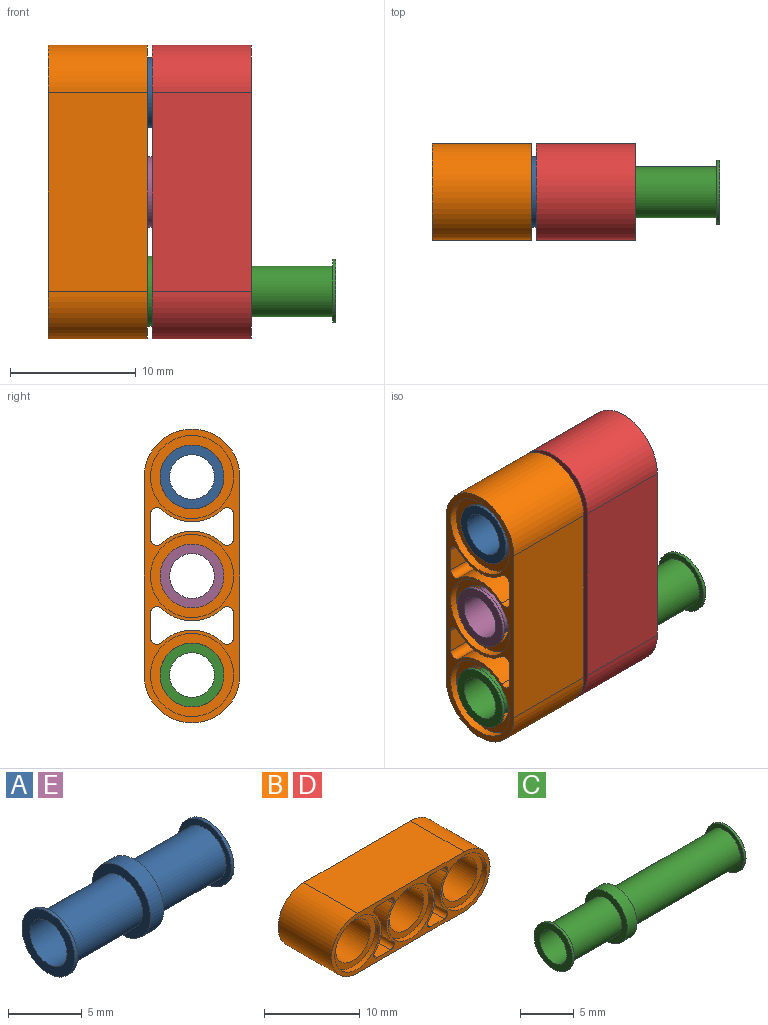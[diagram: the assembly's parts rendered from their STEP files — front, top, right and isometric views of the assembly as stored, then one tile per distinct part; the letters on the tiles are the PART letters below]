
ASSEMBLY  parts=5 mates=4
PART A: 12 faces, bbox 15.2x5.6x5.6 mm
  f0: cylinder r=2.54mm len=5.08mm, axis (-1,0,0), area 4.1mm2, adj f1,f11
  f1: plane 5.08x5.08mm, normal (1,0,0), area 7.3mm2, adj f0,f2
  f2: cylinder r=2.03mm len=6.73mm, axis (-1,0,0), area 85.9mm2, adj f1,f3
  f3: plane 5.59x5.59mm, normal (-1,0,0), area 11.6mm2, adj f2,f4
  f4: cylinder r=2.79mm len=5.59mm, axis (-1,0,0), area 22.3mm2, adj f3,f5
  f5: plane 5.59x5.59mm, normal (1,0,0), area 11.6mm2, adj f4,f6
  f6: cylinder r=2.03mm len=6.73mm, axis (-1,0,0), area 85.9mm2, adj f5,f7
  f7: plane 5.08x5.08mm, normal (-1,0,0), area 7.3mm2, adj f6,f8
  f8: cylinder r=2.54mm len=5.08mm, axis (-1,0,0), area 4.1mm2, adj f7,f9
  f9: plane 5.08x5.08mm, normal (1,0,0), area 10.3mm2, adj f8,f10
  f10: cylinder r=1.78mm len=15.24mm, axis (-1,0,0), area 170.3mm2, adj f9,f11
  f11: plane 5.08x5.08mm, normal (-1,0,0), area 10.3mm2, adj f0,f10
PART B: 37 faces, bbox 23.4x7.9x7.6 mm
  f0: cylinder r=2.54mm len=6.6mm, axis (0,-1,0), area 105.4mm2, adj f11,f32
  f1: plane 7.87x1.97mm, normal (0,0,1), area 15.5mm2, adj f2,f9,f24,f30
  f2: cylinder r=0.51mm len=7.87mm, axis (0,-1,0), area 9.3mm2, adj f1,f3,f9,f30
  f3: cylinder r=3.56mm len=7.87mm, axis (0,-1,0), area 42.5mm2, adj f2,f4,f9,f30
  f4: cylinder r=0.51mm len=7.87mm, axis (0,-1,0), area 9.3mm2, adj f3,f5,f9,f30
  f5: plane 7.87x1.97mm, normal (0,0,-1), area 15.5mm2, adj f4,f9,f22,f30
  f6: plane 15.75x7.87mm, normal (0,0,1), area 124mm2, adj f7,f9,f18,f30
  f7: cylinder r=3.81mm len=7.87mm, axis (0,-1,0), area 94.2mm2, adj f6,f8,f9,f30
  f8: plane 15.75x7.87mm, normal (0,0,-1), area 124mm2, adj f7,f9,f18,f30
  f9: plane 23.37x7.62mm, normal (0,-1,0), area 39.8mm2, adj f1,f2,f3,f4,f5,f6,f7,f8
  f10: cylinder r=3.3mm len=6.6mm, axis (0,-1,0), area 13.2mm2, adj f9,f11
  f11: plane 6.6x6.6mm, normal (0,-1,0), area 14mm2, adj f0,f10
  f12: cylinder r=2.54mm len=6.6mm, axis (0,-1,0), area 105.4mm2, adj f20,f34
  f13: plane 7.87x1.97mm, normal (0,0,1), area 15.5mm2, adj f9,f14,f25,f30
  f14: cylinder r=0.51mm len=7.87mm, axis (0,-1,0), area 9.3mm2, adj f9,f13,f15,f30
  f15: cylinder r=3.56mm len=7.87mm, axis (0,-1,0), area 42.5mm2, adj f9,f14,f16,f30
  f16: cylinder r=0.51mm len=7.87mm, axis (0,-1,0), area 9.3mm2, adj f9,f15,f17,f30
  f17: plane 7.87x1.97mm, normal (0,0,-1), area 15.5mm2, adj f9,f16,f27,f30
  f18: cylinder r=3.81mm len=7.87mm, axis (0,-1,0), area 94.2mm2, adj f6,f8,f9,f30
  f19: cylinder r=3.3mm len=6.6mm, axis (0,-1,0), area 13.2mm2, adj f9,f20
  f20: plane 6.6x6.6mm, normal (0,-1,0), area 14mm2, adj f12,f19
  f21: cylinder r=2.54mm len=6.6mm, axis (0,-1,0), area 105.4mm2, adj f29,f36
  f22: cylinder r=0.51mm len=7.87mm, axis (0,-1,0), area 9.3mm2, adj f5,f9,f23,f30
  f23: cylinder r=3.56mm len=7.87mm, axis (0,-1,0), area 42.5mm2, adj f9,f22,f24,f30
  f24: cylinder r=0.51mm len=7.87mm, axis (0,-1,0), area 9.3mm2, adj f1,f9,f23,f30
  f25: cylinder r=0.51mm len=7.87mm, axis (0,-1,0), area 9.3mm2, adj f9,f13,f26,f30
  f26: cylinder r=3.56mm len=7.87mm, axis (0,-1,0), area 42.5mm2, adj f9,f25,f27,f30
  f27: cylinder r=0.51mm len=7.87mm, axis (0,-1,0), area 9.3mm2, adj f9,f17,f26,f30
  f28: cylinder r=3.3mm len=6.6mm, axis (0,-1,0), area 13.2mm2, adj f9,f29
  f29: plane 6.6x6.6mm, normal (0,-1,0), area 14mm2, adj f21,f28
  f30: plane 23.37x7.62mm, normal (0,1,0), area 39.8mm2, adj f1,f2,f3,f4,f5,f6,f7,f8
  f31: cylinder r=3.3mm len=6.6mm, axis (0,1,0), area 13.2mm2, adj f30,f32
  f32: plane 6.6x6.6mm, normal (0,1,0), area 14mm2, adj f0,f31
  f33: cylinder r=3.3mm len=6.6mm, axis (0,1,0), area 13.2mm2, adj f30,f34
  f34: plane 6.6x6.6mm, normal (0,1,0), area 14mm2, adj f12,f33
  f35: cylinder r=3.3mm len=6.6mm, axis (0,1,0), area 13.2mm2, adj f30,f36
  f36: plane 6.6x6.6mm, normal (0,1,0), area 14mm2, adj f21,f35
PART C: 12 faces, bbox 22.9x5.6x5.6 mm
  f0: cylinder r=2.54mm len=5.08mm, axis (-1,0,0), area 4.1mm2, adj f1,f11
  f1: plane 5.08x5.08mm, normal (1,0,0), area 7.3mm2, adj f0,f2
  f2: cylinder r=2.03mm len=6.73mm, axis (-1,0,0), area 85.9mm2, adj f1,f3
  f3: plane 5.59x5.59mm, normal (-1,0,0), area 11.6mm2, adj f2,f4
  f4: cylinder r=2.79mm len=5.59mm, axis (-1,0,0), area 22.3mm2, adj f3,f5
  f5: plane 5.59x5.59mm, normal (1,0,0), area 11.6mm2, adj f4,f6
  f6: cylinder r=2.03mm len=14.35mm, axis (-1,0,0), area 183.2mm2, adj f5,f7
  f7: plane 5.08x5.08mm, normal (-1,0,0), area 7.3mm2, adj f6,f8
  f8: cylinder r=2.54mm len=5.08mm, axis (-1,0,0), area 4.1mm2, adj f7,f9
  f9: plane 5.08x5.08mm, normal (1,0,0), area 10.3mm2, adj f8,f10
  f10: cylinder r=1.78mm len=22.86mm, axis (-1,0,0), area 255.4mm2, adj f9,f11
  f11: plane 5.08x5.08mm, normal (-1,0,0), area 10.3mm2, adj f0,f10
PART D: same geometry as B
PART E: same geometry as A
PLACE A t=(-8.32,-5.54,-7.7)mm
PLACE B rot(axis=(-0.58,0.58,0.58),120deg) t=(-0.83,-5.54,-15.57)mm
PLACE C rot(axis=(-1,0,0),180deg) t=(-8.7,-5.54,-23.45)mm
PLACE D rot(axis=(0.58,0.58,-0.58),120deg) t=(-0.45,-5.54,-15.57)mm
PLACE E rot(axis=(0,-0.71,0.71),180deg) t=(6.54,-5.54,-15.57)mm
MATE fastened D.f0 <-> C.f0  axis (-1,0,0) through (-0.45,-5.54,-23.45)mm
MATE fastened B.f12 <-> B.f12  axis (-1,0,0) through (-8.07,-5.54,-7.7)mm
MATE fastened E.f0 <-> B.f21  axis (-1,0,0) through (-8.7,-5.54,-15.57)mm
MATE fastened C.f0 <-> B.f0  axis (-1,0,0) through (-8.7,-5.54,-23.45)mm
